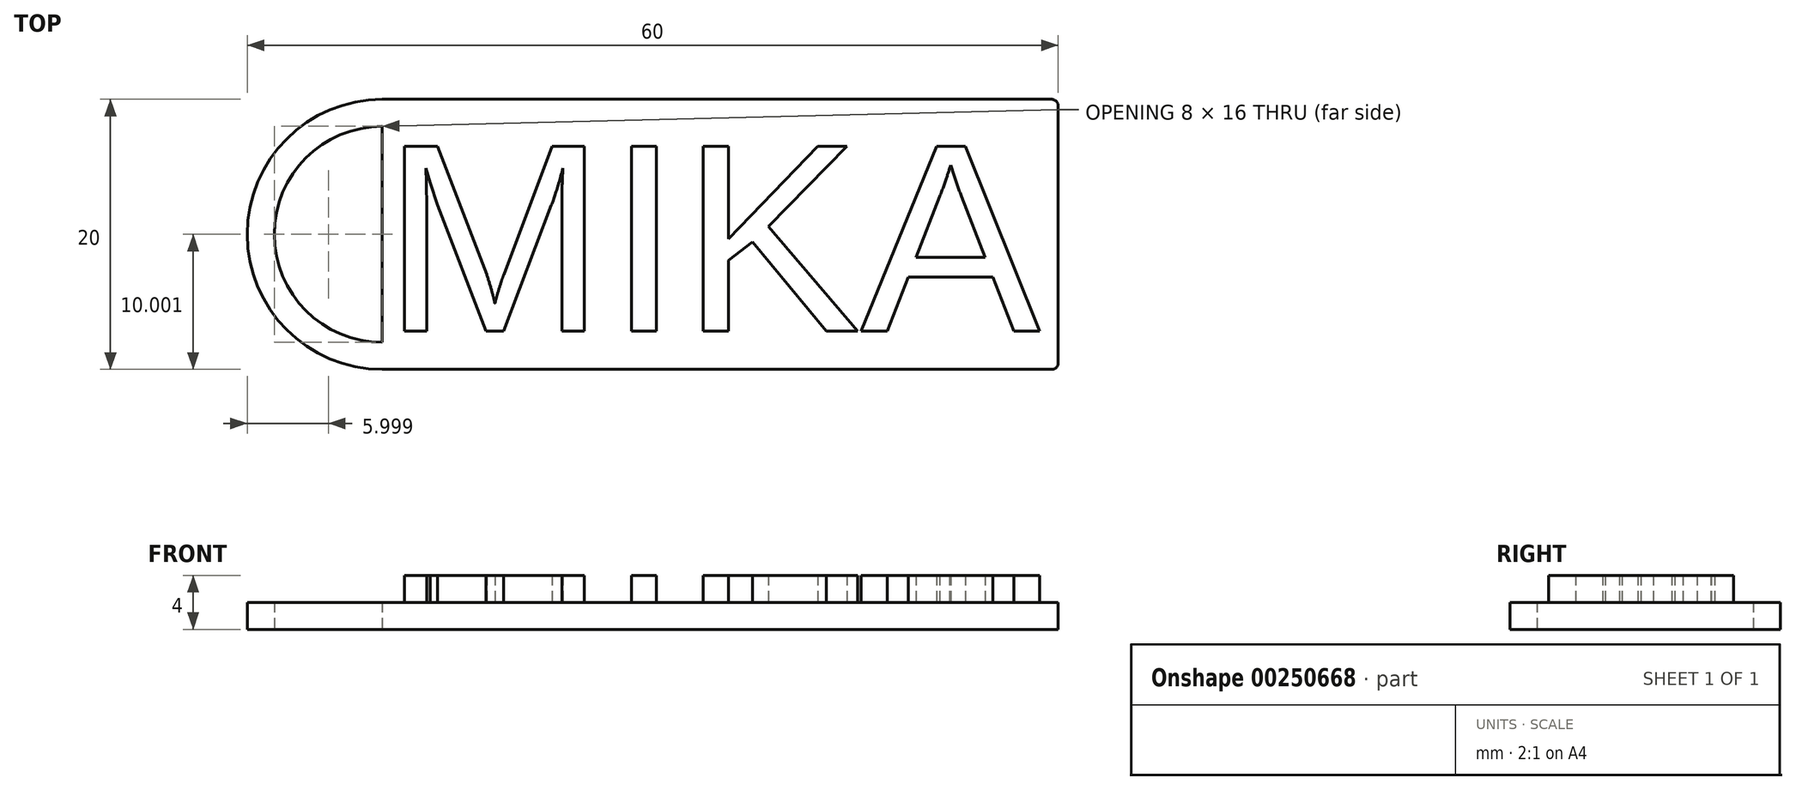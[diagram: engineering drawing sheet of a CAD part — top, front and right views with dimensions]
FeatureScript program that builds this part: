
annotation { "Feature Type Name" : "Feature", "Feature Type Description" : "" }
export const myFeature = defineFeature(function(context is Context, id is Id, definition is map)
    precondition{}
    {
        {
            var Q0;
            Q0=qCreatedBy(makeId("Top.planeOp"),FACE);
            var sketch = newSketch(context, id + "F0", { "sketchPlane" : qUnion([Q0])});
            skLineSegment(sketch, "E0.bottom", {"start": v(-5.27, 3.22) * mm, "end": v(44.73, 3.22) * mm});
            skLineSegment(sketch, "E0.top", {"start": v(-5.27, -16.78) * mm, "end": v(44.73, -16.78) * mm});
            skLineSegment(sketch, "E0.left", {"start": v(-5.27, 3.22) * mm, "end": v(-5.27, -16.78) * mm});
            skLineSegment(sketch, "E0.right", {"start": v(44.73, 3.22) * mm, "end": v(44.73, -16.78) * mm});
            skArc(sketch, "E1", {"start": v(-5.27, 3.22) * mm, "mid": v(-15.27, -6.78) * mm, "end": v(-5.27, -16.78) * mm});
            skArc(sketch, "E2", {"start": v(-5.27, 1.22) * mm, "mid": v(-13.27, -6.78) * mm, "end": v(-5.27, -14.78) * mm});
            skSolve(sketch);
        }
        {
            var Q0;
            Q0=qSketchRegion(id+"F0",true);
            extrude(context, id + "F4", {"entities" : qUnion([Q0]), "depth" : 2 * mm});
        }
        {
            var Q0;
            Q0=makeQuery(id+"F4.opExtrude","SWEPT_EDGE",EDGE,{"disambiguationData":[OSD([sQuery(id+"F0.wireOp",EDGE,"E0.top"),sQuery(id+"F0.wireOp",EDGE,"E0.right")])]});
            var Q1;
            Q1=makeQuery(id+"F4.opExtrude","SWEPT_EDGE",EDGE,{"disambiguationData":[OSD([sQuery(id+"F0.wireOp",EDGE,"E0.bottom"),sQuery(id+"F0.wireOp",EDGE,"E0.right")])]});
            fillet(context, id + "F1", {"entities" : qUnion([Q0, Q1]), "radius" : 0.5 * mm, "tangentPropagation" : true, "allowEdgeOverflow" : false});
        }
        {
            var Q0;
            Q0=makeQuery(id+"F4.opExtrude","CAP_FACE",FACE,{"disambiguationData":[OSD([sQuery(id+"F0.wireOp",EDGE,"E0.bottom"),sQuery(id+"F0.wireOp",EDGE,"E0.top"),sQuery(id+"F0.wireOp",EDGE,"E0.left"),sQuery(id+"F0.wireOp",EDGE,"E0.right"),sQuery(id+"F0.wireOp",EDGE,"E1"),sQuery(id+"F0.wireOp",EDGE,"E2")])],"isStart":false});
            var sketch = newSketch(context, id + "F2", { "sketchPlane" : qUnion([Q0])});
            skText(sketch, "E3", { "text": "MIKA", "fontName": "Arimo-Regular.ttf"});
            skPoint(sketch, "E4", {"position": v(-5.27, -6.78) * mm});
            skPoint(sketch, "E5", {"position": v(44.73, -6.78) * mm});
            const initialGuessF2  = {"E3": [-0.00527, -0.01394, 1, 0, 0.01433]};
            skSetInitialGuess(sketch, initialGuessF2);
            skSolve(sketch);
        }
        {
            var Q0;
            Q0 = qSketchRegion(id + "F2", true);
            extrude(context, id + "F3", {"entities" : qUnion([Q0]), "operationType" : NewBodyOperationType.ADD, "depth" : 2 * mm});
        }
    });
